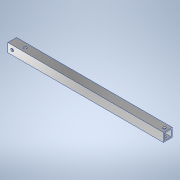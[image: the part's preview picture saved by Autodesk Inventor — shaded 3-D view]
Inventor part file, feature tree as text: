
AUTODESK INVENTOR PART (.ipt)
format: ipt  version: 2020.3 (Build 243373000, 373)  size: 135,168 bytes
history: native  units: mm
features: sketch x3, hole x2, other x1, extrude x1
ambient origin geometry x8: Origin, YZ Plane, XZ Plane, XY Plane, X Axis, Y Axis, Z Axis, Center Point
bodies: Body1 (feature_tree)
feature tree (7):
  other  "ソリッド1"
  extrude  "押し出し1"  Depth=9.0mm
  hole  "穴1"  [1 undecoded]
  hole  "穴2"  [1 undecoded]
  sketch  "スケッチ1"
  sketch  "スケッチ2"
  sketch  "スケッチ3"
note: 2 required parameter values undecoded (feature->parameter linkage not recoverable at this tier; creation-order binding heuristic only, values carry confidence <= 0.55)
